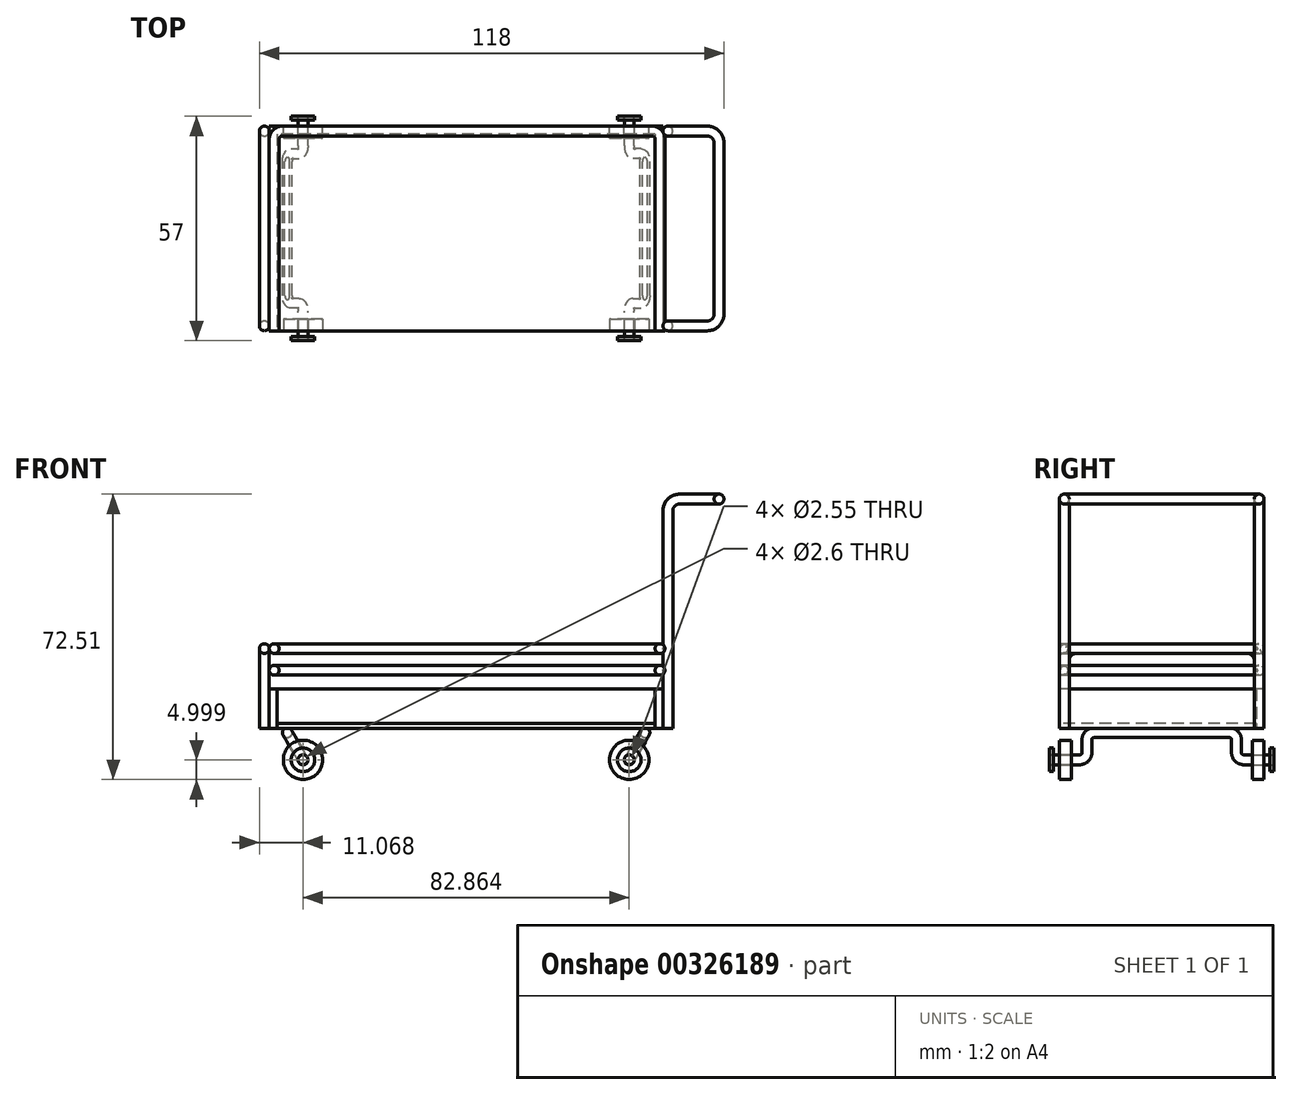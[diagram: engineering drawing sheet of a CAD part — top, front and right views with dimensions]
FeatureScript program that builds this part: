
annotation { "Feature Type Name" : "Feature", "Feature Type Description" : "" }
export const myFeature = defineFeature(function(context is Context, id is Id, definition is map)
    precondition{}
    {
        {
            var Q0;
            Q0=qCreatedBy(makeId("Top.planeOp"),FACE);
            var sketch = newSketch(context, id + "F0", { "sketchPlane" : qUnion([Q0])});
            skLineSegment(sketch, "E0.bottom", {"start": v(48, 25) * mm, "end": v(-48, 25) * mm});
            skLineSegment(sketch, "E0.top", {"start": v(48, -25) * mm, "end": v(-48, -25) * mm});
            skLineSegment(sketch, "E0.left", {"start": v(48, 25) * mm, "end": v(48, -25) * mm});
            skLineSegment(sketch, "E0.right", {"start": v(-48, 25) * mm, "end": v(-48, -25) * mm});
            skPoint(sketch, "E0.middle", {"position": v(0, 0) * mm});
            skSolve(sketch);
        }
        {
            var Q0;
            Q0 = qSketchRegion(id + "F0", true);
            extrude(context, id + "F1", {"entities" : qUnion([Q0]), "depth" : 1.2 * mm});
        }
        {
            var Q0;
            Q0=qCreatedBy(makeId("Top.planeOp"),FACE);
            var sketch = newSketch(context, id + "F2", { "sketchPlane" : qUnion([Q0])});
            skLineSegment(sketch, "E1.0", {"start": v(-48, 25) * mm, "end": v(-48, -25) * mm});
            skLineSegment(sketch, "E1.1", {"start": v(48, 25) * mm, "end": v(-48, 25) * mm});
            skLineSegment(sketch, "E1.2", {"start": v(48, 25) * mm, "end": v(48, -25) * mm});
            skLineSegment(sketch, "E2.0", {"start": v(-50, 27) * mm, "end": v(-50, -25) * mm});
            skLineSegment(sketch, "E2.1", {"start": v(50, 27) * mm, "end": v(-50, 27) * mm});
            skLineSegment(sketch, "E2.2", {"start": v(50, 27) * mm, "end": v(50, -25) * mm});
            skLineSegment(sketch, "E3", {"start": v(-50, -25) * mm, "end": v(-48, -25) * mm});
            skLineSegment(sketch, "E4", {"start": v(48, -25) * mm, "end": v(50, -25) * mm});
            skSolve(sketch);
        }
        {
            var Q0;
            Q0 = qSketchRegion(id + "F2", true);
            extrude(context, id + "F3", {"entities" : qUnion([Q0]), "depth" : 10 * mm});
        }
        {
            var Q0;
            Q0=qCreatedBy(makeId("Top.planeOp"),FACE);
            var sketch = newSketch(context, id + "F4", { "sketchPlane" : qUnion([Q0])});
            skCircle(sketch, "E5", {"center": v(51.25, -23.75) * mm, "radius": 1.25 * mm});
            skSolve(sketch);
        }
        {
            var Q0;
            Q0=qCreatedBy(makeId("Top.planeOp"),FACE);
            var sketch = newSketch(context, id + "F5", { "sketchPlane" : qUnion([Q0])});
            skCircle(sketch, "E6", {"center": v(-51.25, -23.75) * mm, "radius": 1.25 * mm});
            skSolve(sketch);
        }
        {
            var Q0;
            Q0=qCreatedBy(makeId("Right.planeOp"),FACE);
            cPlane(context, id + "F6", {"entities" : qUnion([Q0]), "cplaneType" : CPlaneType.OFFSET, "offset" : 51.25 * mm, "oppositeDirection" : true, "width" : 150 * mm, "height" : 150 * mm});
        }
        {
            var Q0;
            Q0=qCreatedBy(id+"F6.planeOp",FACE);
            var sketch = newSketch(context, id + "F7", { "sketchPlane" : qUnion([Q0])});
            skLineSegment(sketch, "E7", {"start": v(-23.75, 0) * mm, "end": v(-23.75, 17.25) * mm});
            skLineSegment(sketch, "E8", {"start": v(-20.75, 20.25) * mm, "end": v(22.75, 20.25) * mm});
            skLineSegment(sketch, "E9", {"start": v(25.75, 17.25) * mm, "end": v(25.75, 0) * mm});
            skPoint(sketch, "E10.visualSharp", {"position": v(-23.75, 20.25) * mm});
            skArc(sketch, "E10.filletArc", {"start": v(-20.75, 20.25) * mm, "mid": v(-22.87, 19.37) * mm, "end": v(-23.75, 17.25) * mm});
            skPoint(sketch, "E11.visualSharp", {"position": v(25.75, 20.25) * mm});
            skArc(sketch, "E11.filletArc", {"start": v(25.75, 17.25) * mm, "mid": v(24.87, 19.37) * mm, "end": v(22.75, 20.25) * mm});
            skSolve(sketch);
        }
        {
            var Q0;
            Q0=makeQuery(id+"F5.imprint","IMPRINT",FACE,{"disambiguationData":[TD([[makeQuery(id+"F5.imprint","IMPRINT",EDGE,{"derivedFrom":sQuery(id+"F5.wireOp",EDGE,"E6")}),1.0]])]});
            var Q1;
            Q1=sQuery(id+"F7.wireOp",EDGE,"E7");
            var Q2;
            Q2=sQuery(id+"F7.wireOp",EDGE,"E10.filletArc");
            var Q3;
            Q3=sQuery(id+"F7.wireOp",EDGE,"E8");
            var Q4;
            Q4=sQuery(id+"F7.wireOp",EDGE,"E11.filletArc");
            var Q5;
            Q5=sQuery(id+"F7.wireOp",EDGE,"E9");
            sweep(context, id + "F8", {"operationType" : NewBodyOperationType.ADD, "profiles" : qUnion([Q0]), "path" : qUnion([Q1, Q2, Q3, Q4, Q5])});
        }
        {
            var Q0;
            Q0=makeQuery(id+"F3.opExtrude","SWEPT_FACE",FACE,{"disambiguationData":[OSD([sQuery(id+"F2.wireOp",EDGE,"E3")])]});
            var sketch = newSketch(context, id + "F9", { "sketchPlane" : qUnion([Q0])});
            skCircle(sketch, "E12", {"center": v(-48.75, 20.25) * mm, "radius": 1.25 * mm});
            skSolve(sketch);
        }
        {
            var Q0;
            Q0=qCreatedBy(makeId("Top.planeOp"),FACE);
            cPlane(context, id + "F10", {"entities" : qUnion([Q0]), "cplaneType" : CPlaneType.OFFSET, "offset" : 20.25 * mm, "width" : 150 * mm, "height" : 150 * mm});
        }
        {
            var Q0;
            Q0=qCreatedBy(id+"F10.planeOp",FACE);
            var sketch = newSketch(context, id + "F11", { "sketchPlane" : qUnion([Q0])});
            skLineSegment(sketch, "E13", {"start": v(-48.75, -25) * mm, "end": v(-48.75, 23.75) * mm});
            skLineSegment(sketch, "E14", {"start": v(-46.75, 25.75) * mm, "end": v(47.25, 25.75) * mm});
            skLineSegment(sketch, "E15", {"start": v(49.25, 23.75) * mm, "end": v(49.25, -25) * mm});
            skPoint(sketch, "E16.visualSharp", {"position": v(-48.75, 25.75) * mm});
            skArc(sketch, "E16.filletArc", {"start": v(-46.75, 25.75) * mm, "mid": v(-48.16, 25.16) * mm, "end": v(-48.75, 23.75) * mm});
            skPoint(sketch, "E17.visualSharp", {"position": v(49.25, 25.75) * mm});
            skArc(sketch, "E17.filletArc", {"start": v(49.25, 23.75) * mm, "mid": v(48.66, 25.16) * mm, "end": v(47.25, 25.75) * mm});
            skSolve(sketch);
        }
        {
            var Q0;
            Q0=makeQuery(id+"F9.imprint","IMPRINT",FACE,{"disambiguationData":[TD([[makeQuery(id+"F9.imprint","IMPRINT",EDGE,{"derivedFrom":sQuery(id+"F9.wireOp",EDGE,"E12")}),1.0]])]});
            var Q1;
            Q1=sQuery(id+"F11.wireOp",EDGE,"E13");
            var Q2;
            Q2=sQuery(id+"F11.wireOp",EDGE,"E16.filletArc");
            var Q3;
            Q3=sQuery(id+"F11.wireOp",EDGE,"E14");
            var Q4;
            Q4=sQuery(id+"F11.wireOp",EDGE,"E17.filletArc");
            var Q5;
            Q5=sQuery(id+"F11.wireOp",EDGE,"E15");
            sweep(context, id + "F12", {"operationType" : NewBodyOperationType.ADD, "profiles" : qUnion([Q0]), "path" : qUnion([Q1, Q2, Q3, Q4, Q5])});
        }
        {
            var Q0;
            Q0=makeQuery(id+"F3.opExtrude","SWEPT_FACE",FACE,{"disambiguationData":[OSD([sQuery(id+"F2.wireOp",EDGE,"E3")])]});
            var sketch = newSketch(context, id + "F13", { "sketchPlane" : qUnion([Q0])});
            skCircle(sketch, "E18", {"center": v(-48.75, 14.75) * mm, "radius": 1.25 * mm});
            skSolve(sketch);
        }
        {
            var Q0;
            Q0=qCreatedBy(makeId("Top.planeOp"),FACE);
            cPlane(context, id + "F14", {"entities" : qUnion([Q0]), "cplaneType" : CPlaneType.OFFSET, "offset" : 14.75 * mm, "width" : 150 * mm, "height" : 150 * mm});
        }
        {
            var Q0;
            Q0=qCreatedBy(id+"F14.planeOp",FACE);
            var sketch = newSketch(context, id + "F15", { "sketchPlane" : qUnion([Q0])});
            skLineSegment(sketch, "E19.0", {"start": v(-48.75, -25) * mm, "end": v(-48.75, 23.75) * mm});
            skArc(sketch, "E19.1", {"start": v(-46.75, 25.75) * mm, "mid": v(-48.16, 25.16) * mm, "end": v(-48.75, 23.75) * mm});
            skLineSegment(sketch, "E19.2", {"start": v(-46.75, 25.75) * mm, "end": v(47.25, 25.75) * mm});
            skArc(sketch, "E19.3", {"start": v(49.25, 23.75) * mm, "mid": v(48.66, 25.16) * mm, "end": v(47.25, 25.75) * mm});
            skLineSegment(sketch, "E19.4", {"start": v(49.25, 23.75) * mm, "end": v(49.25, -25) * mm});
            skSolve(sketch);
        }
        {
            var Q0;
            Q0=makeQuery(id+"F13.imprint","IMPRINT",FACE,{"disambiguationData":[TD([[makeQuery(id+"F13.imprint","IMPRINT",EDGE,{"derivedFrom":sQuery(id+"F13.wireOp",EDGE,"E18")}),1.0]])]});
            var Q1;
            Q1=sQuery(id+"F15.wireOp",EDGE,"E19.0");
            var Q2;
            Q2=sQuery(id+"F15.wireOp",EDGE,"E19.1");
            var Q3;
            Q3=sQuery(id+"F15.wireOp",EDGE,"E19.2");
            var Q4;
            Q4=sQuery(id+"F15.wireOp",EDGE,"E19.3");
            var Q5;
            Q5=sQuery(id+"F15.wireOp",EDGE,"E19.4");
            sweep(context, id + "F16", {"profiles" : qUnion([Q0]), "path" : qUnion([Q1, Q2, Q3, Q4, Q5])});
        }
        {
            var Q0;
            Q0=makeQuery(id+"F3.opExtrude","SWEPT_FACE",FACE,{"disambiguationData":[OSD([sQuery(id+"F2.wireOp",EDGE,"E4")])]});
            cPlane(context, id + "F17", {"entities" : qUnion([Q0]), "cplaneType" : CPlaneType.OFFSET, "offset" : 1.25 * mm, "oppositeDirection" : true, "width" : 150 * mm, "height" : 150 * mm});
        }
        {
            var Q0;
            Q0=qCreatedBy(id+"F17.planeOp",FACE);
            var sketch = newSketch(context, id + "F18", { "sketchPlane" : qUnion([Q0])});
            skLineSegment(sketch, "E20", {"start": v(51.25, 0) * mm, "end": v(51.25, 55.25) * mm});
            skLineSegment(sketch, "E21", {"start": v(54.25, 58.25) * mm, "end": v(64.25, 58.25) * mm});
            skPoint(sketch, "E22.visualSharp", {"position": v(51.25, 58.25) * mm});
            skArc(sketch, "E22.filletArc", {"start": v(54.25, 58.25) * mm, "mid": v(52.13, 57.37) * mm, "end": v(51.25, 55.25) * mm});
            skSolve(sketch);
        }
        {
            var Q0;
            Q0=makeQuery(id+"F3.opExtrude","SWEPT_FACE",FACE,{"disambiguationData":[OSD([sQuery(id+"F2.wireOp",EDGE,"E2.1")])]});
            cPlane(context, id + "F19", {"entities" : qUnion([Q0]), "cplaneType" : CPlaneType.OFFSET, "offset" : 1.25 * mm, "oppositeDirection" : true, "width" : 150 * mm, "height" : 150 * mm});
        }
        {
            var Q0;
            Q0=qCreatedBy(id+"F19.planeOp",FACE);
            var sketch = newSketch(context, id + "F20", { "sketchPlane" : qUnion([Q0])});
            skLineSegment(sketch, "E23.0", {"start": v(-51.25, 0) * mm, "end": v(-51.25, 55.25) * mm});
            skArc(sketch, "E23.1", {"start": v(-54.25, 58.25) * mm, "mid": v(-52.13, 57.37) * mm, "end": v(-51.25, 55.25) * mm});
            skLineSegment(sketch, "E23.2", {"start": v(-54.25, 58.25) * mm, "end": v(-64.25, 58.25) * mm});
            skSolve(sketch);
        }
        {
            var Q0;
            Q0=qCreatedBy(makeId("Top.planeOp"),FACE);
            cPlane(context, id + "F21", {"entities" : qUnion([Q0]), "cplaneType" : CPlaneType.OFFSET, "offset" : 58.25 * mm, "width" : 150 * mm, "height" : 150 * mm});
        }
        {
            var Q0;
            Q0=qCreatedBy(id+"F21.planeOp",FACE);
            var sketch = newSketch(context, id + "F22", { "sketchPlane" : qUnion([Q0])});
            skLineSegment(sketch, "E24", {"start": v(64.25, 22.75) * mm, "end": v(64.25, -20.75) * mm});
            skLineSegment(sketch, "E25.0", {"start": v(54.25, 25.75) * mm, "end": v(61.25, 25.75) * mm});
            skLineSegment(sketch, "E25.1", {"start": v(54.25, -23.75) * mm, "end": v(61.25, -23.75) * mm});
            skPoint(sketch, "E26.visualSharp", {"position": v(64.25, -23.75) * mm});
            skArc(sketch, "E26.filletArc", {"start": v(61.25, -23.75) * mm, "mid": v(63.37, -22.87) * mm, "end": v(64.25, -20.75) * mm});
            skPoint(sketch, "E27.visualSharp", {"position": v(64.25, 25.75) * mm});
            skArc(sketch, "E27.filletArc", {"start": v(64.25, 22.75) * mm, "mid": v(63.37, 24.87) * mm, "end": v(61.25, 25.75) * mm});
            skSolve(sketch);
        }
        {
            var Q0;
            Q0=makeQuery(id+"F4.imprint","IMPRINT",FACE,{"disambiguationData":[TD([[makeQuery(id+"F4.imprint","IMPRINT",EDGE,{"derivedFrom":sQuery(id+"F4.wireOp",EDGE,"E5")}),1.0]])]});
            var Q1;
            Q1=sQuery(id+"F18.wireOp",EDGE,"E20");
            var Q2;
            Q2=sQuery(id+"F18.wireOp",EDGE,"E22.filletArc");
            var Q3;
            Q3=sQuery(id+"F22.wireOp",EDGE,"E25.1");
            var Q4;
            Q4=sQuery(id+"F22.wireOp",EDGE,"E26.filletArc");
            var Q5;
            Q5=sQuery(id+"F22.wireOp",EDGE,"E24");
            var Q6;
            Q6=sQuery(id+"F22.wireOp",EDGE,"E27.filletArc");
            var Q7;
            Q7=sQuery(id+"F22.wireOp",EDGE,"E25.0");
            var Q8;
            Q8=sQuery(id+"F20.wireOp",EDGE,"E23.1");
            var Q9;
            Q9=sQuery(id+"F20.wireOp",EDGE,"E23.0");
            sweep(context, id + "F23", {"operationType" : NewBodyOperationType.ADD, "profiles" : qUnion([Q0]), "path" : qUnion([Q1, Q2, Q3, Q4, Q5, Q6, Q7, Q8, Q9])});
        }
        {
            var Q0;
            Q0=makeQuery(id+"F3.opExtrude","SWEPT_FACE",FACE,{"disambiguationData":[OSD([sQuery(id+"F2.wireOp",EDGE,"E1.0")])]});
            cPlane(context, id + "F24", {"entities" : qUnion([Q0]), "cplaneType" : CPlaneType.OFFSET, "offset" : 1.25 * mm, "width" : 150 * mm, "height" : 150 * mm});
        }
        {
            var Q0;
            Q0=qCreatedBy(id+"F24.planeOp",FACE);
            var sketch = newSketch(context, id + "F25", { "sketchPlane" : qUnion([Q0])});
            skLineSegment(sketch, "E28.0", {"start": v(25, 1.2) * mm, "end": v(-25, 1.2) * mm});
            skSolve(sketch);
        }
        {
            var Q0;
            Q0=sQuery(id+"F25.wireOp",EDGE,"E28.0");
            cPlane(context, id + "F26", {"entities" : qUnion([Q0]), "cplaneType" : CPlaneType.LINE_ANGLE, "offset" : 25 * mm, "angle" : 120 * degree, "width" : 150 * mm, "height" : 150 * mm});
        }
        {
            var Q0;
            Q0=qCreatedBy(id+"F26.planeOp",FACE);
            var sketch = newSketch(context, id + "F27", { "sketchPlane" : qUnion([Q0])});
            skLineSegment(sketch, "E29", {"start": v(29.5, 13.78) * mm, "end": v(22, 13.78) * mm});
            skLineSegment(sketch, "E30", {"start": v(20, 15.78) * mm, "end": v(20, 19.78) * mm});
            skLineSegment(sketch, "E31", {"start": v(18, 21.78) * mm, "end": v(-16, 21.78) * mm});
            skLineSegment(sketch, "E32", {"start": v(-18, 19.78) * mm, "end": v(-18, 15.78) * mm});
            skLineSegment(sketch, "E33", {"start": v(-20, 13.78) * mm, "end": v(-27.5, 13.78) * mm});
            skPoint(sketch, "E34.visualSharp", {"position": v(20, 13.78) * mm});
            skArc(sketch, "E34.filletArc", {"start": v(20, 15.78) * mm, "mid": v(20.59, 14.36) * mm, "end": v(22, 13.78) * mm});
            skPoint(sketch, "E35.visualSharp", {"position": v(20, 21.78) * mm});
            skArc(sketch, "E35.filletArc", {"start": v(20, 19.78) * mm, "mid": v(19.41, 21.2) * mm, "end": v(18, 21.78) * mm});
            skPoint(sketch, "E36.visualSharp", {"position": v(-18, 21.78) * mm});
            skArc(sketch, "E36.filletArc", {"start": v(-16, 21.78) * mm, "mid": v(-17.41, 21.2) * mm, "end": v(-18, 19.78) * mm});
            skPoint(sketch, "E37.visualSharp", {"position": v(-18, 13.78) * mm});
            skArc(sketch, "E37.filletArc", {"start": v(-20, 13.78) * mm, "mid": v(-18.59, 14.36) * mm, "end": v(-18, 15.78) * mm});
            skSolve(sketch);
        }
        {
            var Q0;
            Q0=sQuery(id+"F27.wireOp",VERTEX,"E33.end");
            var Q1;
            Q1=sQuery(id+"F27.wireOp",EDGE,"E33");
            cPlane(context, id + "F28", {"entities" : qUnion([Q0, Q1]), "cplaneType" : CPlaneType.LINE_POINT, "offset" : 25 * mm, "width" : 150 * mm, "height" : 150 * mm});
        }
        {
            var Q0;
            Q0=qCreatedBy(id+"F28.planeOp",FACE);
            var sketch = newSketch(context, id + "F29", { "sketchPlane" : qUnion([Q0])});
            skCircle(sketch, "E38", {"center": v(-41.43, -8.01) * mm, "radius": 1.25 * mm});
            skSolve(sketch);
        }
        {
            var Q0;
            Q0=makeQuery(id+"F29.imprint","IMPRINT",FACE,{"disambiguationData":[TD([[makeQuery(id+"F29.imprint","IMPRINT",EDGE,{"derivedFrom":sQuery(id+"F29.wireOp",EDGE,"E38")}),1.0]])]});
            var Q1;
            Q1=sQuery(id+"F27.wireOp",EDGE,"E33");
            var Q2;
            Q2=sQuery(id+"F27.wireOp",EDGE,"E37.filletArc");
            var Q3;
            Q3=sQuery(id+"F27.wireOp",EDGE,"E32");
            var Q4;
            Q4=sQuery(id+"F27.wireOp",EDGE,"E36.filletArc");
            var Q5;
            Q5=sQuery(id+"F27.wireOp",EDGE,"E31");
            var Q6;
            Q6=sQuery(id+"F27.wireOp",EDGE,"E35.filletArc");
            var Q7;
            Q7=sQuery(id+"F27.wireOp",EDGE,"E30");
            var Q8;
            Q8=sQuery(id+"F27.wireOp",EDGE,"E34.filletArc");
            var Q9;
            Q9=sQuery(id+"F27.wireOp",EDGE,"E29");
            sweep(context, id + "F30", {"profiles" : qUnion([Q0]), "path" : qUnion([Q1, Q2, Q3, Q4, Q5, Q6, Q7, Q8, Q9])});
        }
        {
            var Q0;
            Q0=makeQuery(id+"F30.opSweep","SWEPT_BODY",BODY,{"disambiguationData":[OSD([sQuery(id+"F27.wireOp",EDGE,"E29"),sQuery(id+"F29.wireOp",EDGE,"E38")])]});
            var Q1;
            Q1=qCreatedBy(makeId("Right.planeOp"),FACE);
            mirror(context, id + "F31", {"operationType" : NewBodyOperationType.ADD, "entities" : qUnion([Q0]), "mirrorPlane" : qUnion([Q1])});
        }
        {
            var Q0;
            Q0=makeQuery(id+"F30.opSweep","CAP_FACE",FACE,{"disambiguationData":[OSD([sQuery(id+"F27.wireOp",VERTEX,"E33.end"),sQuery(id+"F29.wireOp",EDGE,"E38")])],"isStart":true});
            var sketch = newSketch(context, id + "F32", { "sketchPlane" : qUnion([Q0])});
            skCircle(sketch, "E39", {"center": v(-41.43, -8.01) * mm, "radius": 1.27 * mm});
            skCircle(sketch, "E40", {"center": v(-41.43, -8.01) * mm, "radius": 3 * mm});
            skSolve(sketch);
        }
        {
            var Q0;
            Q0 = qSketchRegion(id + "F32", true);
            extrude(context, id + "F33", {"entities" : qUnion([Q0]), "oppositeDirection" : true, "depth" : 1 * mm});
        }
        {
            var Q0;
            Q0=makeQuery(id+"F1.opExtrude","SWEPT_FACE",FACE,{"disambiguationData":[OSD([sQuery(id+"F0.wireOp",EDGE,"E0.top")])]});
            var sketch = newSketch(context, id + "F34", { "sketchPlane" : qUnion([Q0])});
            skCircle(sketch, "E41", {"center": v(-41.43, -8.01) * mm, "radius": 5 * mm});
            skCircle(sketch, "E42", {"center": v(-41.43, -8.01) * mm, "radius": 1.3 * mm});
            skSolve(sketch);
        }
        {
            var Q0;
            Q0 = qSketchRegion(id + "F34", true);
            extrude(context, id + "F35", {"entities" : qUnion([Q0]), "oppositeDirection" : true, "depth" : 3 * mm});
        }
        {
            var Q0;
            Q0=qCreatedBy(makeId("Front.planeOp"),FACE);
            cPlane(context, id + "F36", {"entities" : qUnion([Q0]), "cplaneType" : CPlaneType.OFFSET, "offset" : 1 * mm, "oppositeDirection" : true, "width" : 150 * mm, "height" : 150 * mm});
        }
        {
            var Q0;
            Q0=makeQuery(id+"F35.opExtrude","SWEPT_BODY",BODY,{"disambiguationData":[OSD([sQuery(id+"F34.wireOp",EDGE,"E41"),sQuery(id+"F34.wireOp",EDGE,"E42")])]});
            var Q1;
            Q1=makeQuery(id+"F33.opExtrude","SWEPT_BODY",BODY,{"disambiguationData":[OSD([sQuery(id+"F32.wireOp",EDGE,"E39"),sQuery(id+"F32.wireOp",EDGE,"E40")])]});
            var Q2;
            Q2=qCreatedBy(id+"F36.planeOp",FACE);
            mirror(context, id + "F37", {"entities" : qUnion([Q0, Q1]), "mirrorPlane" : qUnion([Q2])});
        }
        {
            var Q0;
            Q0=makeQuery(id+"F33.opExtrude","SWEPT_BODY",BODY,{"disambiguationData":[OSD([sQuery(id+"F32.wireOp",EDGE,"E39"),sQuery(id+"F32.wireOp",EDGE,"E40")])]});
            var Q1;
            Q1=makeQuery(id+"F35.opExtrude","SWEPT_BODY",BODY,{"disambiguationData":[OSD([sQuery(id+"F34.wireOp",EDGE,"E41"),sQuery(id+"F34.wireOp",EDGE,"E42")])]});
            var Q2;
            Q2=makeQuery(id+"F37.opPattern","COPY",BODY,{"derivedFrom":makeQuery(id+"F33.opExtrude","SWEPT_BODY",BODY,{"disambiguationData":[OSD([sQuery(id+"F32.wireOp",EDGE,"E39"),sQuery(id+"F32.wireOp",EDGE,"E40")])]}),"instanceName":"1"});
            var Q3;
            Q3=makeQuery(id+"F37.opPattern","COPY",BODY,{"derivedFrom":makeQuery(id+"F35.opExtrude","SWEPT_BODY",BODY,{"disambiguationData":[OSD([sQuery(id+"F34.wireOp",EDGE,"E41"),sQuery(id+"F34.wireOp",EDGE,"E42")])]}),"instanceName":"1"});
            var Q4;
            Q4=qCreatedBy(makeId("Right.planeOp"),FACE);
            mirror(context, id + "F38", {"entities" : qUnion([Q0, Q1, Q2, Q3]), "mirrorPlane" : qUnion([Q4])});
        }
    });
